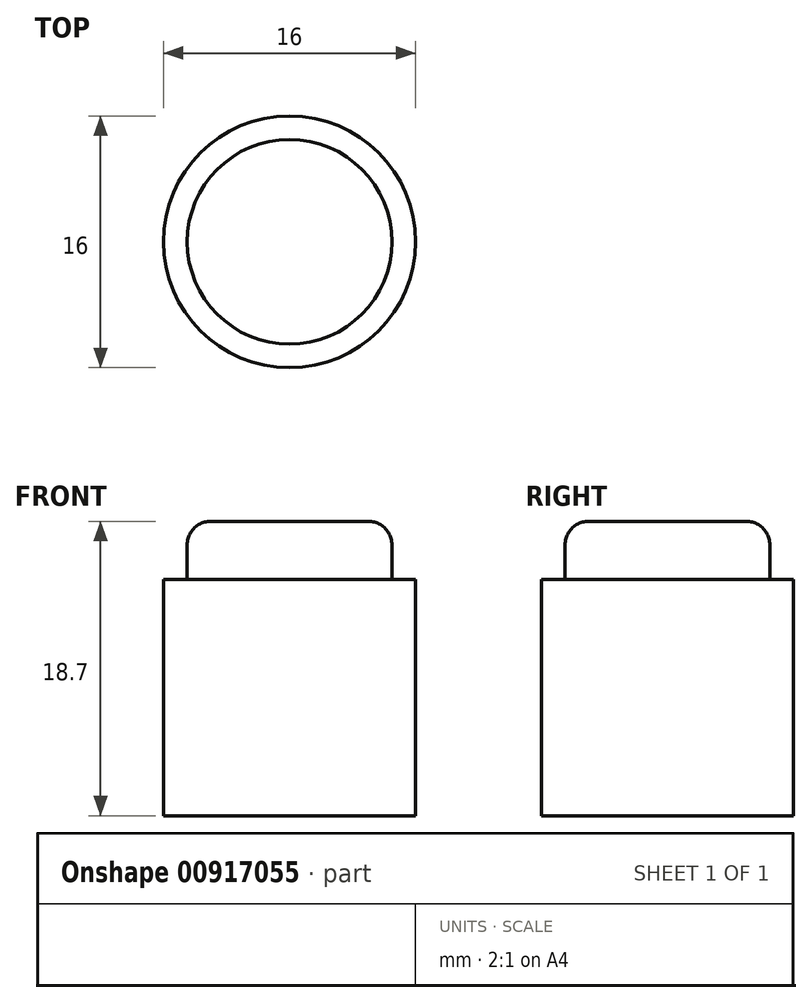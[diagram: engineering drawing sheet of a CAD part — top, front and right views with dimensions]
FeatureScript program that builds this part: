
annotation { "Feature Type Name" : "Feature", "Feature Type Description" : "" }
export const myFeature = defineFeature(function(context is Context, id is Id, definition is map)
    precondition{}
    {
        {
            var Q0;
            Q0=qCreatedBy(makeId("Top.planeOp"),FACE);
            var sketch = newSketch(context, id + "F0", { "sketchPlane" : qUnion([Q0])});
            skCircle(sketch, "E0", {"center": v(0, 0) * mm, "radius": 6.5 * mm});
            skSolve(sketch);
        }
        {
            var Q0;
            Q0=makeQuery(id+"F0.imprint","IMPRINT",FACE,{"disambiguationData":[TD([[makeQuery(id+"F0.imprint","IMPRINT",EDGE,{"derivedFrom":sQuery(id+"F0.wireOp",EDGE,"E0")}),1.0]])]});
            extrude(context, id + "F1", {"entities" : qUnion([Q0]), "depth" : 3.7 * mm, "offsetDistance" : 25 * mm});
        }
        {
            var Q0;
            Q0=makeQuery(id+"F1.opExtrude","CAP_EDGE",EDGE,{"disambiguationData":[OSD([sQuery(id+"F0.wireOp",EDGE,"E0")])],"isStart":false});
            fillet(context, id + "F2", {"entities" : qUnion([Q0]), "radius" : 1.5 * mm, "tangentPropagation" : true, "allowEdgeOverflow" : false});
        }
        {
            var Q0;
            Q0=qCreatedBy(makeId("Top.planeOp"),FACE);
            var sketch = newSketch(context, id + "F3", { "sketchPlane" : qUnion([Q0])});
            skCircle(sketch, "E1", {"center": v(0, 0) * mm, "radius": 8 * mm});
            skSolve(sketch);
        }
        {
            var Q0;
            Q0=makeQuery(id+"F3.imprint","IMPRINT",FACE,{"disambiguationData":[TD([[makeQuery(id+"F3.imprint","IMPRINT",EDGE,{"derivedFrom":sQuery(id+"F3.wireOp",EDGE,"E1")}),1.0]])]});
            extrude(context, id + "F4", {"entities" : qUnion([Q0]), "operationType" : NewBodyOperationType.ADD, "oppositeDirection" : true, "depth" : 15 * mm, "offsetDistance" : 25 * mm});
        }
    });
